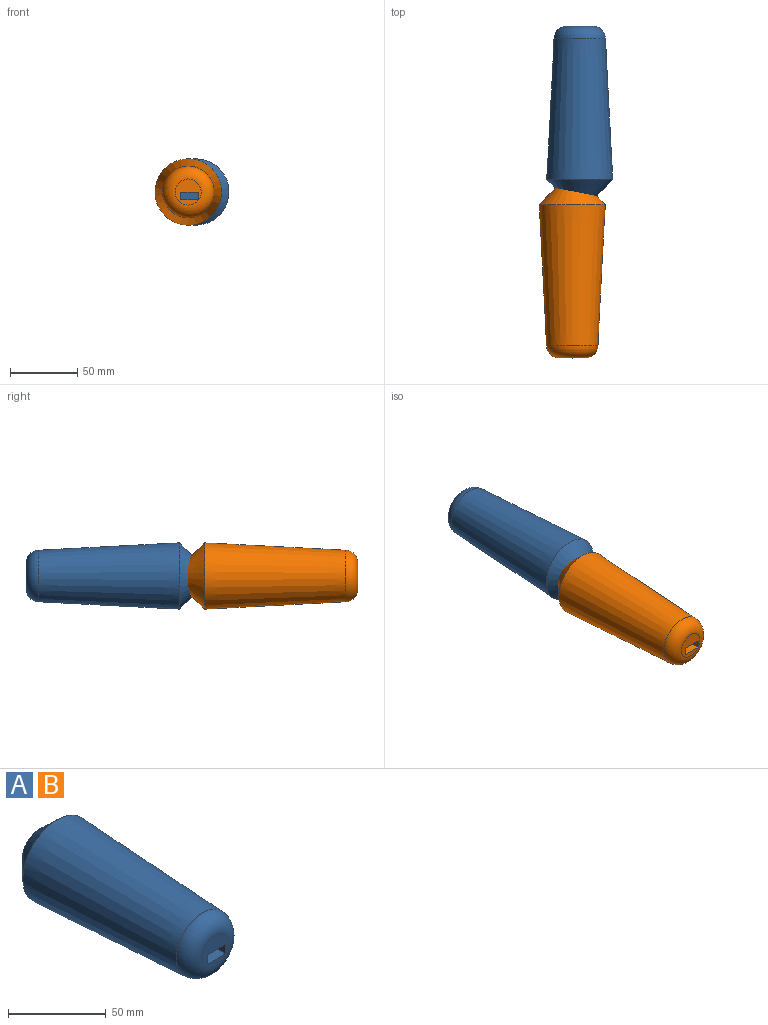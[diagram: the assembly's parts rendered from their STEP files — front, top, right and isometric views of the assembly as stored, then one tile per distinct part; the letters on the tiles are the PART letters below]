
ASSEMBLY  parts=2 mates=1
PART A: 9 faces, bbox 49.5x127x49.5 mm
  f0: plane 19.41x19.41mm, normal (0,-1,0), area 217.4mm2, adj f3,f5,f6,f7,f8
  f1: cone r=25.4mm half-angle=3deg, axis (0,1,0), area 14558.6mm2, adj f3,f4
  f2: plane 25.4x25.4mm, normal (0,1,0), area 428.2mm2, adj f4,f5,f6,f7,f8
  f3: torus R=9.71mm, axis (0,-1,0), area 1422.2mm2, adj f0,f1
  f4: cone r=24.74mm half-angle=43.5deg, axis (0,-1,0), area 2056.3mm2, adj f1,f2
  f5: plane 127x5.86mm, normal (1,0,0), area 743.8mm2, adj f0,f2,f6,f7
  f6: plane 127x13.41mm, normal (0,0,-1), area 1702.4mm2, adj f0,f2,f5,f8
  f7: plane 127x13.41mm, normal (0,0,1), area 1702.4mm2, adj f0,f2,f5,f8
  f8: plane 127x5.86mm, normal (-1,0,0), area 743.8mm2, adj f0,f2,f6,f7
PART B: same geometry as A
PLACE A rot(axis=(1,0,0),180deg) t=(3.27,31.7,4.87)mm
PLACE B t=(-2.4,38.04,4.87)mm
MATE fastened A.f2 <-> B.f1  axis (0,-1,0) through (-2.4,31.7,4.87)mm
